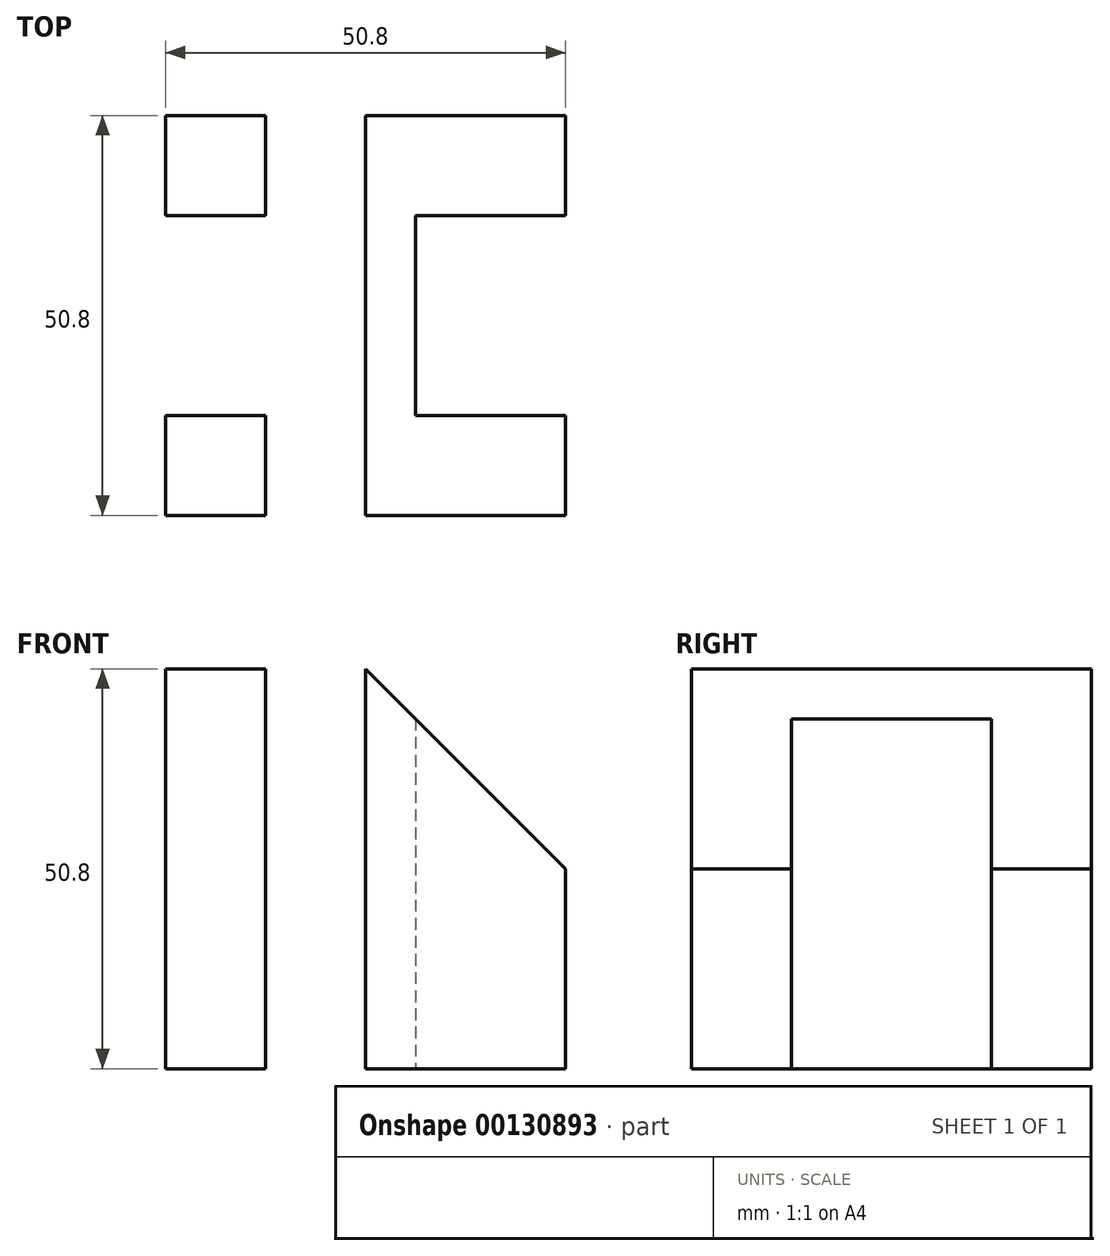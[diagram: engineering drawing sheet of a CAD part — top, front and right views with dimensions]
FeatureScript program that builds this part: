
annotation { "Feature Type Name" : "Feature", "Feature Type Description" : "" }
export const myFeature = defineFeature(function(context is Context, id is Id, definition is map)
    precondition{}
    {
        {
            var Q0;
            Q0=qCreatedBy(makeId("Top.planeOp"),FACE);
            var sketch = newSketch(context, id + "F0", { "sketchPlane" : qUnion([Q0])});
            skLineSegment(sketch, "E0.bottom", {"start": v(0, 0) * mm, "end": v(50.8, 0) * mm});
            skLineSegment(sketch, "E0.top", {"start": v(0, 50.8) * mm, "end": v(50.8, 50.8) * mm});
            skLineSegment(sketch, "E0.left", {"start": v(0, 0) * mm, "end": v(0, 50.8) * mm});
            skLineSegment(sketch, "E0.right", {"start": v(50.8, 0) * mm, "end": v(50.8, 50.8) * mm});
            skLineSegment(sketch, "E1.bottom", {"start": v(50.8, 38.1) * mm, "end": v(31.75, 38.1) * mm});
            skLineSegment(sketch, "E1.top", {"start": v(50.8, 12.7) * mm, "end": v(31.75, 12.7) * mm});
            skLineSegment(sketch, "E1.left", {"start": v(50.8, 38.1) * mm, "end": v(50.8, 12.7) * mm});
            skLineSegment(sketch, "E1.right", {"start": v(31.75, 38.1) * mm, "end": v(31.75, 12.7) * mm});
            skLineSegment(sketch, "E2.bottom", {"start": v(0, 50.8) * mm, "end": v(12.7, 50.8) * mm});
            skLineSegment(sketch, "E2.top", {"start": v(0, 38.1) * mm, "end": v(12.7, 38.1) * mm});
            skLineSegment(sketch, "E2.left", {"start": v(0, 50.8) * mm, "end": v(0, 38.1) * mm});
            skLineSegment(sketch, "E2.right", {"start": v(12.7, 50.8) * mm, "end": v(12.7, 38.1) * mm});
            skLineSegment(sketch, "E3.bottom", {"start": v(0, 0) * mm, "end": v(12.7, 0) * mm});
            skLineSegment(sketch, "E3.top", {"start": v(0, 12.7) * mm, "end": v(12.7, 12.7) * mm});
            skLineSegment(sketch, "E3.left", {"start": v(0, 0) * mm, "end": v(0, 12.7) * mm});
            skLineSegment(sketch, "E3.right", {"start": v(12.7, 0) * mm, "end": v(12.7, 12.7) * mm});
            skLineSegment(sketch, "E4", {"start": v(25.4, 50.8) * mm, "end": v(25.4, 0) * mm});
            skSolve(sketch);
        }
        {
            var Q0;
            {var subQ5=sQuery(id+"F0.wireOp",EDGE,"E1.top");Q0=makeQuery(id+"F0.imprint","IMPRINT",FACE,{"disambiguationData":[TD([[makeQuery(id+"F0.imprint","IMPRINT",EDGE,{"derivedFrom":subQ5}),1.0]])]});}
            var Q1;
            {var subQ5=sQuery(id+"F0.wireOp",EDGE,"E1.bottom");Q1=makeQuery(id+"F0.imprint","IMPRINT",FACE,{"disambiguationData":[TD([[makeQuery(id+"F0.imprint","IMPRINT",EDGE,{"derivedFrom":subQ5}),-1.0]])]});}
            var Q2;
            Q2=makeQuery(id+"F0.imprint","IMPRINT",FACE,{"disambiguationData":[TD([[makeQuery(id+"F0.imprint","IMPRINT",EDGE,{"derivedFrom":sQuery(id+"F0.wireOp",EDGE,"E0.left")}),-1.0]])]});
            extrude(context, id + "F1", {"entities" : qUnion([Q0, Q1, Q2]), "endBound" : BoundingType.SYMMETRIC, "depth" : 50.8 * mm});
        }
        {
            var Q0;
            Q0=makeQuery(id+"F1.opExtrude","SWEPT_FACE",FACE,{"disambiguationData":[OSD([sQuery(id+"F0.wireOp",EDGE,"E0.bottom")])]});
            var sketch = newSketch(context, id + "F2", { "sketchPlane" : qUnion([Q0])});
            skLineSegment(sketch, "E5", {"start": v(50.8, 0) * mm, "end": v(25.4, 25.4) * mm});
            skSolve(sketch);
        }
        {
            var Q0;
            Q0=qSketchRegion(id+"F2",true);
            var Q1;
            {var subQ0=sQuery(id+"F2.wireOp",EDGE,"E5");Q1=makeQuery(id+"F2.imprint","IMPRINT",FACE,{"disambiguationData":[TD([[makeQuery(id+"F2.imprint","IMPRINT",EDGE,{"derivedFrom":subQ0}),-1.0]])]});}
            extrude(context, id + "F3", {"entities" : qUnion([Q0, Q1]), "operationType" : NewBodyOperationType.REMOVE, "endBound" : BoundingType.THROUGH_ALL, "oppositeDirection" : true, "depth" : 25.4 * mm});
        }
    });
